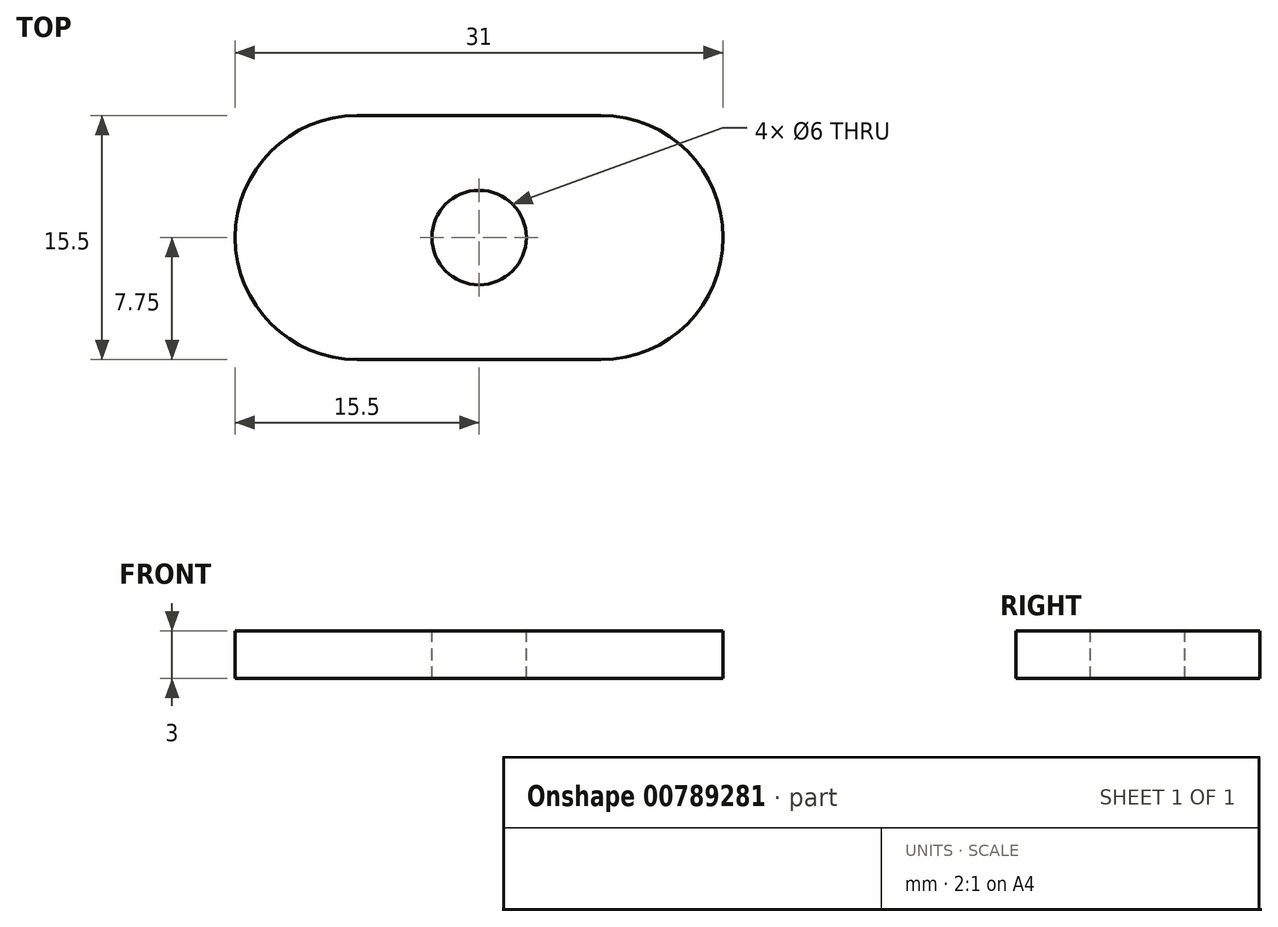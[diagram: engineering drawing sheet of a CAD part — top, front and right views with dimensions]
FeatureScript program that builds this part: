
annotation { "Feature Type Name" : "Feature", "Feature Type Description" : "" }
export const myFeature = defineFeature(function(context is Context, id is Id, definition is map)
    precondition{}
    {
        {
            var Q0;
            Q0=qCreatedBy(makeId("Top.planeOp"),FACE);
            var sketch = newSketch(context, id + "F0", { "sketchPlane" : qUnion([Q0])});
            skLineSegment(sketch, "E0.bottom", {"start": v(-7.75, 7.75) * mm, "end": v(7.75, 7.75) * mm});
            skLineSegment(sketch, "E0.top", {"start": v(-7.75, -7.75) * mm, "end": v(7.75, -7.75) * mm});
            skPoint(sketch, "E0.middle", {"position": v(0, 0) * mm});
            skArc(sketch, "E1", {"start": v(7.75, 7.75) * mm, "mid": v(15.5, 0) * mm, "end": v(7.75, -7.75) * mm});
            skArc(sketch, "E2", {"start": v(-7.75, 7.75) * mm, "mid": v(-15.5, 0) * mm, "end": v(-7.75, -7.75) * mm});
            skCircle(sketch, "E3", {"center": v(0, 0) * mm, "radius": 3 * mm});
            skSolve(sketch);
        }
        {
            var Q0;
            Q0=makeQuery(id+"F0.imprint","IMPRINT",FACE,{"disambiguationData":[TD([[makeQuery(id+"F0.imprint","IMPRINT",EDGE,{"derivedFrom":sQuery(id+"F0.wireOp",EDGE,"E0.bottom")}),-1.0]])]});
            var Q1;
            Q1=makeQuery(id+"F0.imprint","IMPRINT",FACE,{"disambiguationData":[TD([[makeQuery(id+"F0.imprint","IMPRINT",EDGE,{"derivedFrom":sQuery(id+"F0.wireOp",EDGE,"E3")}),1.0]])]});
            extrude(context, id + "F1", {"entities" : qUnion([Q0, Q1]), "depth" : 3 * mm, "offsetDistance" : 25 * mm});
        }
        {
            var Q0;
            Q0=makeQuery(id+"F1.opExtrude","CAP_FACE",FACE,{"disambiguationData":[OSD([sQuery(id+"F0.wireOp",EDGE,"E0.bottom"),sQuery(id+"F0.wireOp",EDGE,"E0.top"),sQuery(id+"F0.wireOp",EDGE,"E1"),sQuery(id+"F0.wireOp",EDGE,"E2")])],"isStart":false});
            var sketch = newSketch(context, id + "F2", { "sketchPlane" : qUnion([Q0])});
            skCircle(sketch, "E4", {"center": v(0, 0) * mm, "radius": 3 * mm});
            skSolve(sketch);
        }
        {
            var Q0;
            Q0=makeQuery(id+"F2.imprint","IMPRINT",FACE,{"disambiguationData":[TD([[makeQuery(id+"F2.imprint","IMPRINT",EDGE,{"derivedFrom":sQuery(id+"F2.wireOp",EDGE,"E4")}),1.0]])]});
            extrude(context, id + "F3", {"entities" : qUnion([Q0]), "operationType" : NewBodyOperationType.REMOVE, "oppositeDirection" : true, "depth" : 25 * mm, "offsetDistance" : 25 * mm});
        }
    });
